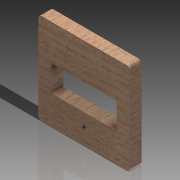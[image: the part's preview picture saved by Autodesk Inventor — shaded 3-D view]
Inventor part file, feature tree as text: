
AUTODESK INVENTOR PART (.ipt)
format: ipt  version: 2014 SP1 (Build 180222100, 222)  size: 157,184 bytes
history: native  units: mm
features: sketch x3, extrude x2, hole x1, fillet x1
ambient origin geometry x8: Origin, YZ Plane, XZ Plane, XY Plane, X Axis, Y Axis, Z Axis, Center Point
bodies: Volumenkörper1 (feature_tree)
feature tree (7):
  extrude  "Extrusion1"  Depth=140.0mm
  hole  "Bohrung1"  [1 undecoded]
  fillet  "Rundung1"  Radius=15.0mm
  extrude  "Extrusion2"  Depth=18.0mm
  sketch  "Skizze1"  dims[d0=140.0mm d1=140.0mm]
  sketch  "Skizze2"  dims[d2=18.0mm d3=0.0mm d4=15.0mm d5=15.0mm]
  sketch  "Skizze3"  dims[d6=15.0mm d7=15.0mm d8=9.0mm d9=9.0mm d10=9.0mm d11=9.0mm d12=2.0mm d13=6.0mm d14=5.0mm d15=2.0mm d16=90.0deg d17=8.0mm d18=20.594885mm d19=5.0mm d20=20.0mm d23=100.0mm d24=40.0mm d25=45.0mm d26=5.0mm d27=70.0mm d28=25.0mm d29=18.0mm d30=0.0mm]
note: 1 required parameter value undecoded (feature->parameter linkage not recoverable at this tier; creation-order binding heuristic only, values carry confidence <= 0.55)
